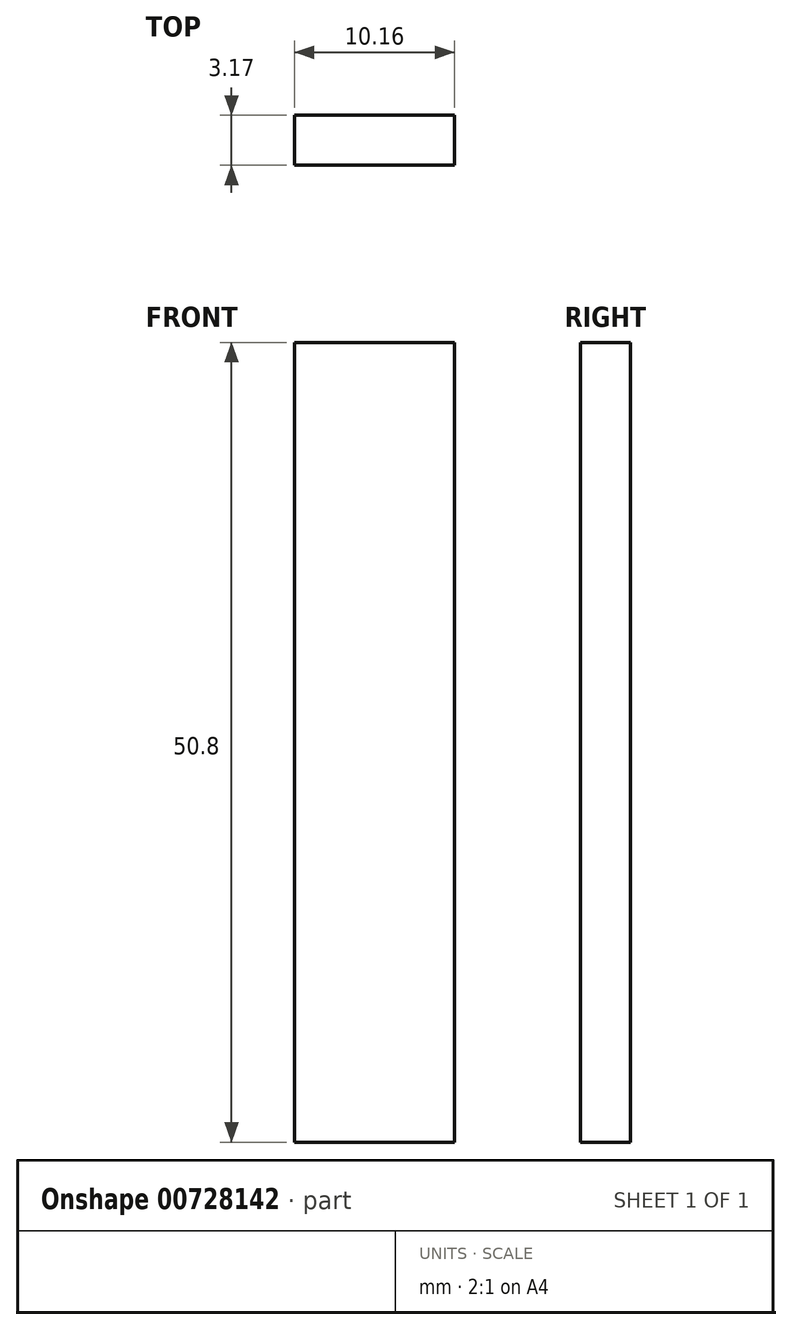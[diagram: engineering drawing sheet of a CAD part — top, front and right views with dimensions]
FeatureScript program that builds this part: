
annotation { "Feature Type Name" : "Feature", "Feature Type Description" : "" }
export const myFeature = defineFeature(function(context is Context, id is Id, definition is map)
    precondition{}
    {
        {
            var Q0;
            Q0=qCreatedBy(makeId("Front.planeOp"),FACE);
            var sketch = newSketch(context, id + "F0", { "sketchPlane" : qUnion([Q0])});
            skLineSegment(sketch, "E0.bottom", {"start": v(5.08, 25.4) * mm, "end": v(-5.08, 25.4) * mm});
            skLineSegment(sketch, "E0.top", {"start": v(5.08, -25.4) * mm, "end": v(-5.08, -25.4) * mm});
            skLineSegment(sketch, "E0.left", {"start": v(5.08, 25.4) * mm, "end": v(5.08, -25.4) * mm});
            skLineSegment(sketch, "E0.right", {"start": v(-5.08, 25.4) * mm, "end": v(-5.08, -25.4) * mm});
            skPoint(sketch, "E0.middle", {"position": v(0, 0) * mm});
            skSolve(sketch);
        }
        {
            var Q0;
            Q0=makeQuery(id+"F0.imprint","IMPRINT",FACE,{"disambiguationData":[TD([[makeQuery(id+"F0.imprint","IMPRINT",EDGE,{"derivedFrom":sQuery(id+"F0.wireOp",EDGE,"E0.bottom")}),1.0]])]});
            extrude(context, id + "F1", {"entities" : qUnion([Q0]), "depth" : 3.17 * mm, "offsetDistance" : 25.4 * mm});
        }
    });
